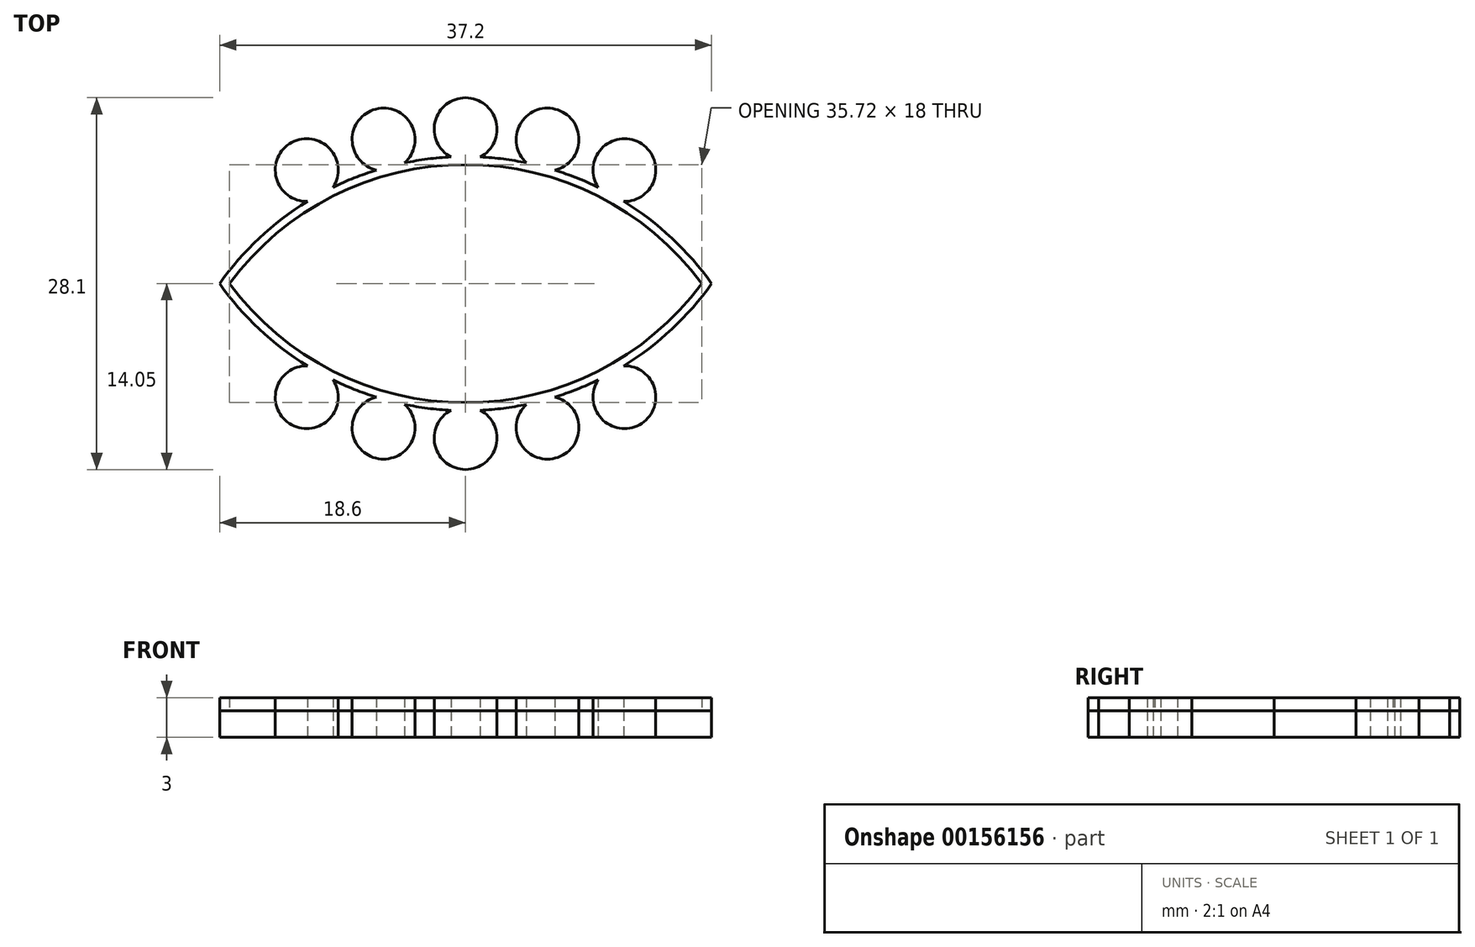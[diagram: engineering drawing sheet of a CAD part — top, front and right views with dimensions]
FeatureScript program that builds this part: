
annotation { "Feature Type Name" : "Feature", "Feature Type Description" : "" }
export const myFeature = defineFeature(function(context is Context, id is Id, definition is map)
    precondition{}
    {
        {
            var Q0;
            Q0=qCreatedBy(makeId("Top.planeOp"),FACE);
            var sketch = newSketch(context, id + "F0", { "sketchPlane" : qUnion([Q0])});
            skLineSegment(sketch, "E0", {"start": v(-15.04, 9.6) * mm, "end": v(18.06, 9.6) * mm, "construction": true});
            skLineSegment(sketch, "E1", {"start": v(18.6, 8.9) * mm, "end": v(18.6, -7.07) * mm, "construction": true});
            skLineSegment(sketch, "E2", {"start": v(-18.6, 9.63) * mm, "end": v(-18.6, -9.63) * mm, "construction": true});
            skArc(sketch, "E3", {"start": v(18.6, 0) * mm, "mid": v(0, 9.6) * mm, "end": v(-18.6, 0) * mm});
            skPoint(sketch, "E3.startSnap0", {"position": v(-18.6, 0) * mm});
            skArc(sketch, "E4.0", {"start": v(17.86, 0) * mm, "mid": v(0, 9) * mm, "end": v(-17.86, 0) * mm});
            skCircle(sketch, "E5", {"center": v(0, 11.68) * mm, "radius": 2.38 * mm});
            skCircle(sketch, "E6", {"center": v(6.2, 10.9) * mm, "radius": 2.38 * mm});
            skCircle(sketch, "E7", {"center": v(12.01, 8.59) * mm, "radius": 2.38 * mm});
            skArc(sketch, "E8.0", {"start": v(18.1, 0.18) * mm, "mid": v(0, 9.3) * mm, "end": v(-18.1, 0.18) * mm, "construction": true});
            skCircle(sketch, "E9.MirrorC", {"center": v(-6.2, 10.9) * mm, "radius": 2.38 * mm});
            skCircle(sketch, "E10.MirrorC", {"center": v(-12.01, 8.59) * mm, "radius": 2.38 * mm});
            skLineSegment(sketch, "E11.MirrorCS", {"start": v(-15.04, -9.6) * mm, "end": v(18.06, -9.6) * mm, "construction": true});
            skCircle(sketch, "E12.MirrorC", {"center": v(-12.01, -8.59) * mm, "radius": 2.38 * mm});
            skCircle(sketch, "E13.MirrorC", {"center": v(-6.2, -10.9) * mm, "radius": 2.38 * mm});
            skArc(sketch, "E14.MirrorCS", {"start": v(18.6, 0) * mm, "mid": v(0, -9.6) * mm, "end": v(-18.6, 0) * mm});
            skArc(sketch, "E15.MirrorCS", {"start": v(17.86, 0) * mm, "mid": v(0, -9) * mm, "end": v(-17.86, 0) * mm});
            skArc(sketch, "E16.MirrorCS", {"start": v(18.1, -0.18) * mm, "mid": v(0, -9.3) * mm, "end": v(-18.1, -0.18) * mm, "construction": true});
            skCircle(sketch, "E17.MirrorC", {"center": v(12.01, -8.59) * mm, "radius": 2.38 * mm});
            skCircle(sketch, "E18.MirrorC", {"center": v(6.2, -10.9) * mm, "radius": 2.38 * mm});
            skCircle(sketch, "E19.MirrorC", {"center": v(0, -11.68) * mm, "radius": 2.38 * mm});
            skSolve(sketch);
        }
        {
            var Q0;
            Q0 = qSketchRegion(id + "F0", true);
            var Q1;
            Q1=makeQuery(id+"F0.imprint","IMPRINT",FACE,{"disambiguationData":[TD([[makeQuery(id+"F0.imprint","IMPRINT",EDGE,{"derivedFrom":sQuery(id+"F0.wireOp",EDGE,"E4.0")}),1.0]])]});
            extrude(context, id + "F1", {"entities" : qUnion([Q0, Q1]), "depth" : 2 * mm});
        }
        {
            var Q0;
            Q0 = qSketchRegion(id + "F0", true);
            extrude(context, id + "F2", {"entities" : qUnion([Q0]), "depth" : 1 * mm});
        }
        {
            var Q0;
            Q0=makeQuery(id+"F2.opExtrude","SWEPT_BODY",BODY,{"disambiguationData":[OSD([sQuery(id+"F0.wireOp",EDGE,"E3"),sQuery(id+"F0.wireOp",EDGE,"E4.0"),sQuery(id+"F0.wireOp",EDGE,"E5"),sQuery(id+"F0.wireOp",EDGE,"E6"),sQuery(id+"F0.wireOp",EDGE,"E7"),sQuery(id+"F0.wireOp",EDGE,"E9.MirrorC"),sQuery(id+"F0.wireOp",EDGE,"E10.MirrorC"),sQuery(id+"F0.wireOp",EDGE,"E12.MirrorC"),sQuery(id+"F0.wireOp",EDGE,"E13.MirrorC"),sQuery(id+"F0.wireOp",EDGE,"E14.MirrorCS"),sQuery(id+"F0.wireOp",EDGE,"E15.MirrorCS"),sQuery(id+"F0.wireOp",EDGE,"E17.MirrorC"),sQuery(id+"F0.wireOp",EDGE,"E18.MirrorC"),sQuery(id+"F0.wireOp",EDGE,"E19.MirrorC")])]});
            transform(context, id + "F3", {"entities" : qUnion([Q0]), "transformType" : TransformType.TRANSLATION_3D, "dx" : 0 * mm, "dy" : 0 * mm, "dz" : 2 * mm, "makeCopy" : false});
        }
    });
